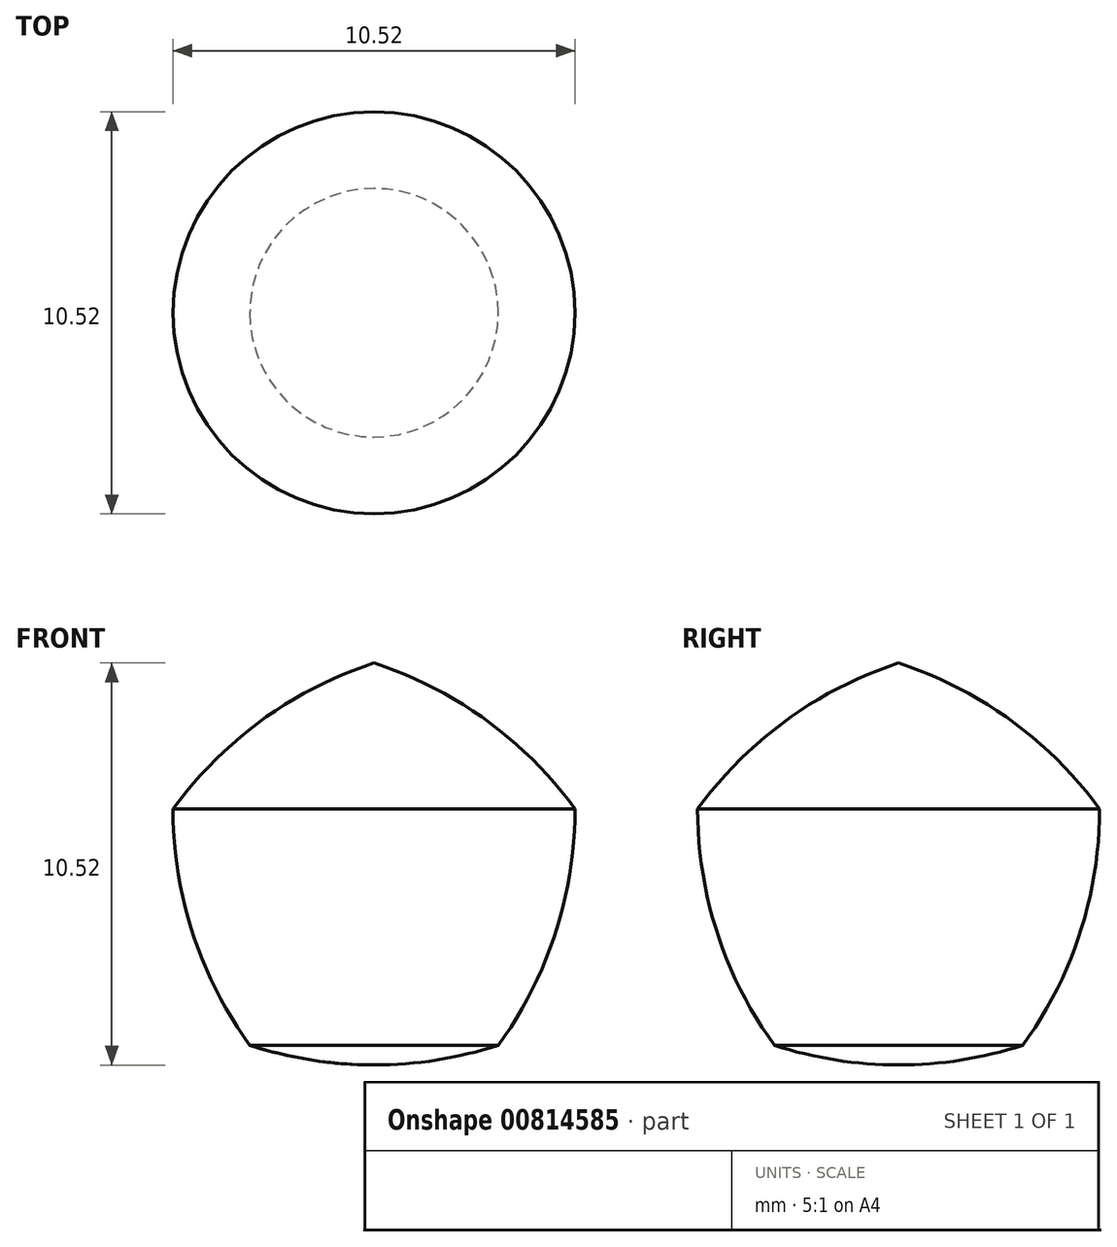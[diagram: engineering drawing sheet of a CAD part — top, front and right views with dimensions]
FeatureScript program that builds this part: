
annotation { "Feature Type Name" : "Feature", "Feature Type Description" : "" }
export const myFeature = defineFeature(function(context is Context, id is Id, definition is map)
    precondition{}
    {
        {
            var Q0;
            Q0=qCreatedBy(makeId("Front.planeOp"),FACE);
            var sketch = newSketch(context, id + "F0", { "sketchPlane" : qUnion([Q0])});
            skArc(sketch, "E0.cCircle", {"start": v(0, -4.47) * mm, "mid": v(4.47, 0) * mm, "end": v(0, 4.47) * mm, "construction": true});
            skLineSegment(sketch, "E0.0", {"start": v(3.25, -4.47) * mm, "end": v(0, -4.47) * mm});
            skLineSegment(sketch, "E0.3", {"start": v(0, 5.53) * mm, "end": v(5.26, 1.7) * mm});
            skLineSegment(sketch, "E0.4", {"start": v(5.26, 1.7) * mm, "end": v(3.25, -4.47) * mm});
            skPoint(sketch, "E0.0.midPoint", {"position": v(0, -4.47) * mm});
            skArc(sketch, "E1", {"start": v(0, -4.99) * mm, "mid": v(1.64, -4.86) * mm, "end": v(3.25, -4.47) * mm});
            skArc(sketch, "E2", {"start": v(3.25, -4.47) * mm, "mid": v(4.74, -1.54) * mm, "end": v(5.26, 1.7) * mm});
            skArc(sketch, "E3", {"start": v(5.26, 1.7) * mm, "mid": v(2.93, 4.03) * mm, "end": v(0, 5.53) * mm});
            skLineSegment(sketch, "E4", {"start": v(0, 6.8) * mm, "end": v(0, -5.88) * mm});
            skPoint(sketch, "E4.endSnap0", {"position": v(0, -4.99) * mm});
            skSolve(sketch);
        }
        {
            var Q0;
            Q0 = qSketchRegion(id + "F0", true);
            var Q1;
            Q1=sQuery(id+"F0.wireOp",EDGE,"E4");
            revolve(context, id + "F1", {"surfaceOperationType" : NewSurfaceOperationType.NEW, "entities" : qUnion([Q0]), "axis" : qUnion([Q1]), "revolveType" : RevolveType.FULL});
        }
    });
